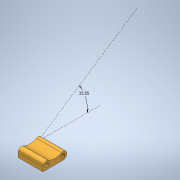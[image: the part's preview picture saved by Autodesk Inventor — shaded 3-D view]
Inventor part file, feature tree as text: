
AUTODESK INVENTOR PART (.ipt)
format: ipt  version: 2020 (Build 240168000, 168)  size: 264,704 bytes
history: native  units: in
note: dims shown in document units (in); Inventor stores cm internally (conversion verified against a paired STEP export)
features: sketch x7, extrude x6, projected_geometry x4, other x3, fillet x2
ambient origin geometry x8: Origin, YZ Plane, XZ Plane, XY Plane, X Axis, Y Axis, Z Axis, Center Point
bodies: Solid1 (feature_tree)
feature tree (22):
  other  "Assembly4.iam"
  other  "Kauri modular session 5 mount.ipt:1"
  other  "session 5.ipt:1"
  extrude  "Extrusion1"  Depth=0.3937in TaperAngle=0.0deg
  extrude  "Extrusion2"  Depth=1.0in TaperAngle=0.0deg
  extrude  "Extrusion3"  Depth=0.3937in TaperAngle=0.0deg
  fillet  "Fillet1"  Radius=0.2362in
  fillet  "Fillet2"  Radius=0.0394in
  extrude  "Extrusion4"  Depth=0.3937in
  extrude  "Extrusion6"  Depth=0.0197in
  sketch  "Sketch7"  dims[d20=0.0197in d23=0.3937in d24=0.0in]
  extrude  "Extrusion7"  Depth=0.3937in TaperAngle=0.0deg
  sketch  "Sketch1"  dims[d0=0.3937in d1=1.0in d2=0.0in]
  projected_geometry  "Projected Loop1"
  sketch  "Sketch2"  dims[d3=0.5906in d4=1.0in d5=0.0in]
  sketch  "Sketch3"  dims[d6=0.9843in d7=0.3937in d8=0.0in d9=0.2362in d10=0.0394in]
  projected_geometry  "Projected Loop2"
  sketch  "Sketch4"  dims[d12=0.0197in d15=0.3937in d16=0.0in d17=0.0197in]
  projected_geometry  "Projected Loop3"
  sketch  "Sketch6"  dims[d18=0.0197in d19=0.0197in]
  sketch  "Sketch8"  dims[d25=0.2305in d26=0.3937in d27=0.0in d28=0.0197in d29=0.0344in]
  projected_geometry  "Projected Loop5"
